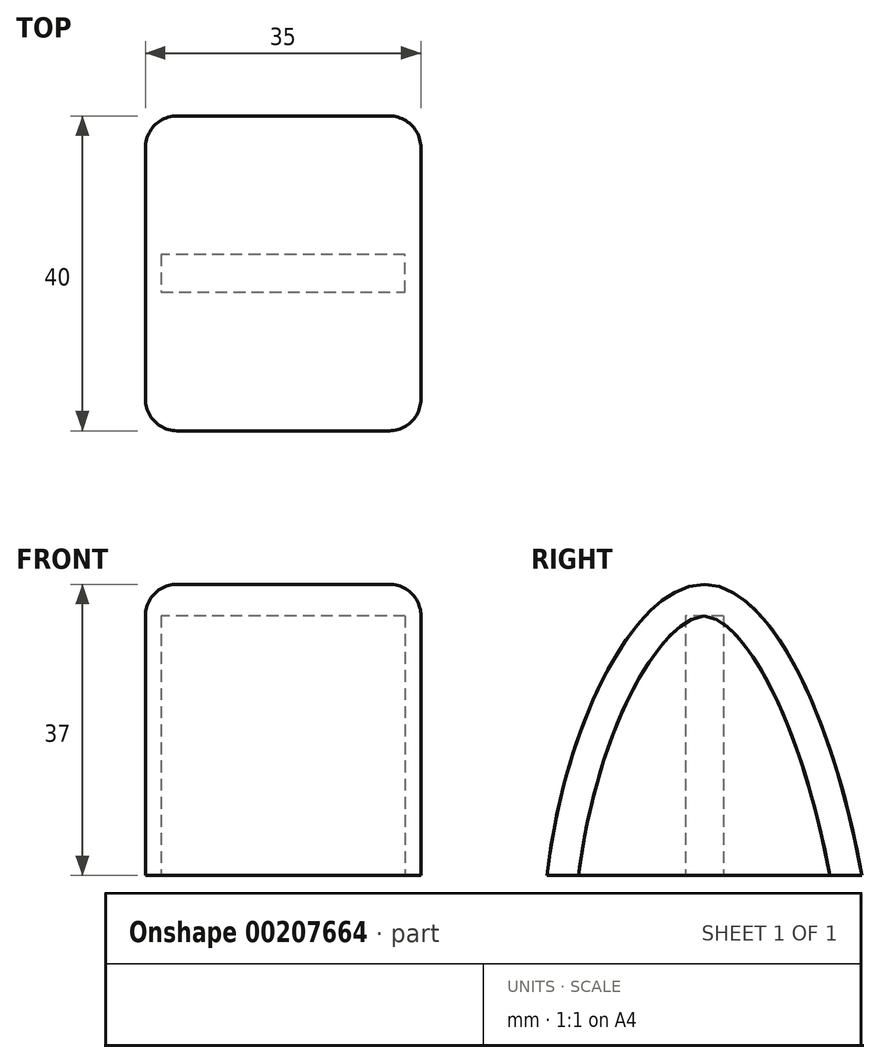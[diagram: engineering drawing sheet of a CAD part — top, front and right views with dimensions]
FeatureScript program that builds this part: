
annotation { "Feature Type Name" : "Feature", "Feature Type Description" : "" }
export const myFeature = defineFeature(function(context is Context, id is Id, definition is map)
    precondition{}
    {
        {
            assignVariable(context, id + "F0", {"name" : "T", "anyValue" : 2 * mm});
        }
        {
            assignVariable(context, id + "F1", {"name" : "H", "anyValue" : 33 * mm});
        }
        {
            assignVariable(context, id + "F2", {"name" : "W", "anyValue" : 31 * mm});
        }
        {
            var Q0;
            Q0=qCreatedBy(makeId("Right.planeOp"),FACE);
            var sketch = newSketch(context, id + "F3", { "sketchPlane" : qUnion([Q0])});
            skLineSegment(sketch, "E0", {"start": v(0, 0) * mm, "end": v(0, 37) * mm});
            skLineSegment(sketch, "E1", {"start": v(0, 0) * mm, "end": v(-20, 0) * mm});
            skLineSegment(sketch, "E2", {"start": v(0, 0) * mm, "end": v(20, 0) * mm});
            skFitSpline(sketch, "E3", {"points": [v(20, 0) * mm, v(0, 37) * mm, v(-20, 0) * mm], "startDerivative": vector(-21.16, 119.08) * mm, "endDerivative": vector(-14.23, -120.32) * mm});
            skSolve(sketch);
        }
        {
            var Q0;
            Q0=makeQuery(id+"F3.imprint","IMPRINT",FACE,{"disambiguationData":[TD([[makeQuery(id+"F3.imprint","IMPRINT",EDGE,{"derivedFrom":sQuery(id+"F3.wireOp",EDGE,"E0")}),1.0]])]});
            var Q1;
            {var subQ0=sQuery(id+"F3.wireOp",EDGE,"E0");Q1=makeQuery(id+"F3.imprint","IMPRINT",FACE,{"disambiguationData":[TD([[makeQuery(id+"F3.imprint","IMPRINT",EDGE,{"derivedFrom":subQ0}),-1.0]])]});}
            extrude(context, id + "F4", {"entities" : qUnion([Q0, Q1]), "depth" : getVariable(context, 'W') + getVariable(context, 'T') * 2});
        }
        {
            var Q0;
            Q0=makeQuery(id+"F4.opExtrude","SWEPT_FACE",FACE,{"disambiguationData":[OSD([sQuery(id+"F3.wireOp",EDGE,"E1"),sQuery(id+"F3.wireOp",EDGE,"E2")])]});
            var sketch = newSketch(context, id + "F5", { "sketchPlane" : qUnion([Q0])});
            skLineSegment(sketch, "E4", {"start": v(0, 0) * mm, "end": v(2, 0) * mm});
            skLineSegment(sketch, "E5", {"start": v(2, 0) * mm, "end": v(2, 2.4) * mm});
            skLineSegment(sketch, "E6", {"start": v(2, 2.4) * mm, "end": v(33, 2.4) * mm});
            skLineSegment(sketch, "E7", {"start": v(33, 2.4) * mm, "end": v(33, 0) * mm});
            skLineSegment(sketch, "E8", {"start": v(33, 0) * mm, "end": v(33, -2.4) * mm});
            skLineSegment(sketch, "E9", {"start": v(33, -2.4) * mm, "end": v(2, -2.4) * mm});
            skLineSegment(sketch, "E10", {"start": v(2, -2.4) * mm, "end": v(2, 0) * mm});
            skSolve(sketch);
        }
        {
            var Q0;
            Q0 = qSketchRegion(id + "F5", true);
            extrude(context, id + "F6", {"entities" : qUnion([Q0]), "operationType" : NewBodyOperationType.REMOVE, "oppositeDirection" : true, "depth" : getVariable(context, 'H')});
        }
        {
            var Q0;
            Q0=makeQuery(id+"F4.opExtrude","CAP_EDGE",EDGE,{"disambiguationData":[OSD([sQuery(id+"F3.wireOp",EDGE,"eYyFGdXp-TI5g-rbJe-cQfW-34mV812zxmXJ")])],"isStart":true});
            var Q1;
            Q1=makeQuery(id+"F4.opExtrude","CAP_EDGE",EDGE,{"disambiguationData":[OSD([sQuery(id+"F3.wireOp",EDGE,"eYyFGdXp-TI5g-rbJe-cQfW-34mV812zxmXJ")])],"isStart":false});
            var Q2;
            Q2=makeQuery(id+"F4.opExtrude","SWEPT_EDGE",EDGE,{"disambiguationData":[OSD([sQuery(id+"F3.wireOp",EDGE,"E0"),sQuery(id+"F3.wireOp",EDGE,"eYyFGdXp-TI5g-rbJe-cQfW-34mV812zxmXJ")])]});
            var Q3;
            Q3=makeQuery(id+"F4.opExtrude","CAP_EDGE",EDGE,{"disambiguationData":[OSD([sQuery(id+"F3.wireOp",EDGE,"E3")])],"isStart":false});
            var Q4;
            Q4=makeQuery(id+"F4.opExtrude","CAP_EDGE",EDGE,{"disambiguationData":[OSD([sQuery(id+"F3.wireOp",EDGE,"E3")])],"isStart":true});
            fillet(context, id + "F7", {"entities" : qUnion([Q0, Q1, Q2, Q3, Q4]), "radius" : getVariable(context, 'T') * 2, "tangentPropagation" : true, "allowEdgeOverflow" : false});
        }
    });
